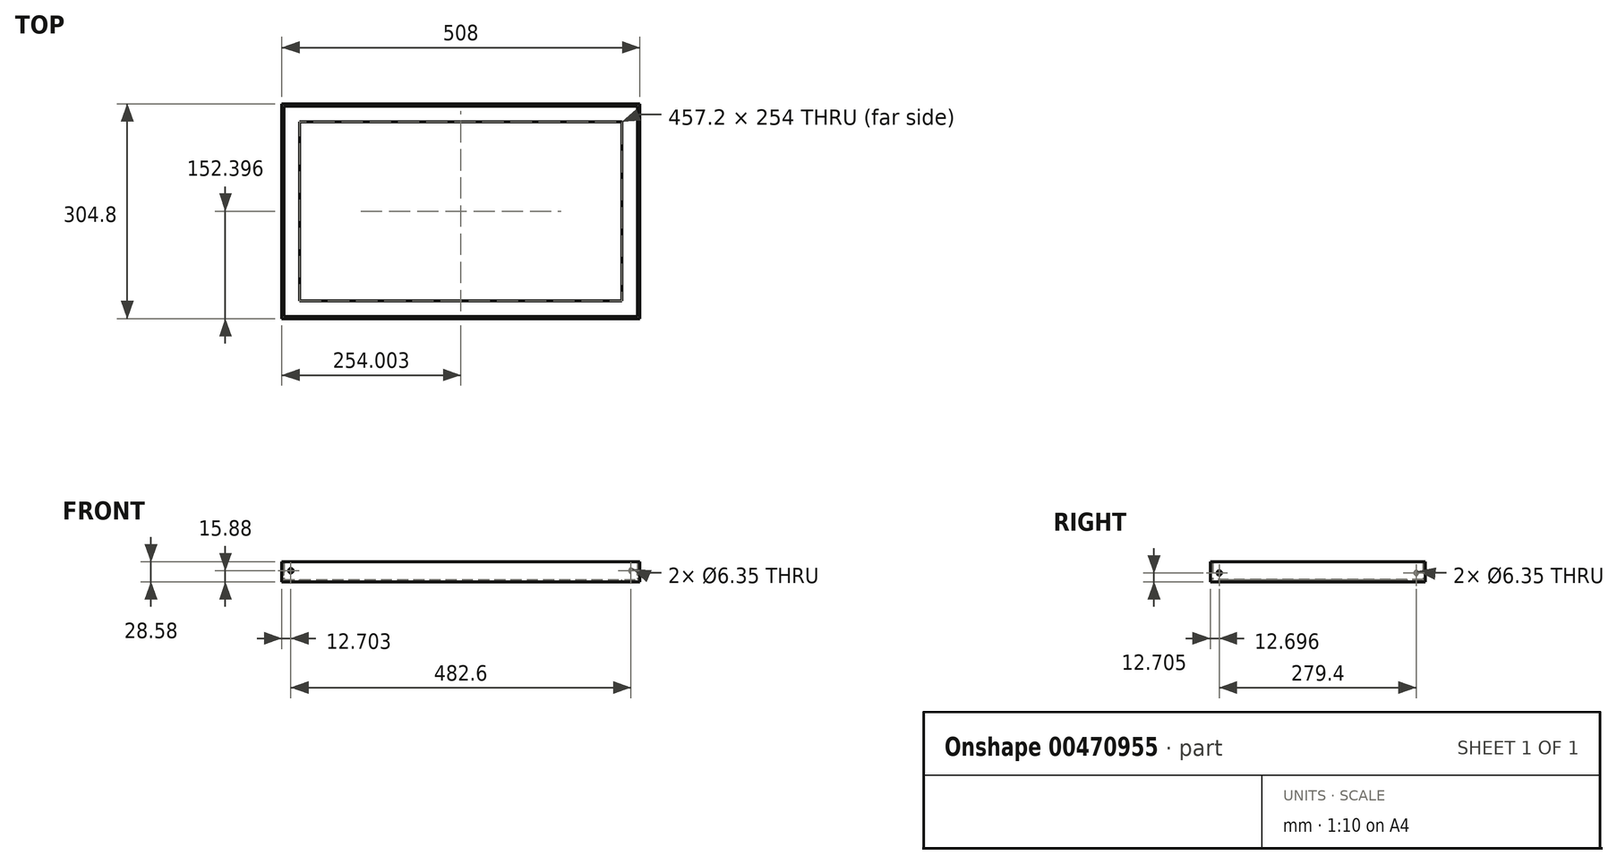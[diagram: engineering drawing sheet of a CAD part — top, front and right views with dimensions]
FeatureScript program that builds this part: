
annotation { "Feature Type Name" : "Feature", "Feature Type Description" : "" }
export const myFeature = defineFeature(function(context is Context, id is Id, definition is map)
    precondition{}
    {
        {
            var Q0;
            Q0=qCreatedBy(makeId("Top.planeOp"),FACE);
            var sketch = newSketch(context, id + "F0", { "sketchPlane" : qUnion([Q0])});
            skLineSegment(sketch, "E0.bottom", {"start": v(-258.98, 164.35) * mm, "end": v(249.02, 164.35) * mm});
            skLineSegment(sketch, "E0.top", {"start": v(-258.98, -140.45) * mm, "end": v(249.02, -140.45) * mm});
            skLineSegment(sketch, "E0.left", {"start": v(-258.98, 164.35) * mm, "end": v(-258.98, -140.45) * mm});
            skLineSegment(sketch, "E0.right", {"start": v(249.02, 164.35) * mm, "end": v(249.02, -140.45) * mm});
            skLineSegment(sketch, "E1.0", {"start": v(-255.8, 164.35) * mm, "end": v(-255.8, -140.45) * mm});
            skLineSegment(sketch, "E2.0", {"start": v(-258.98, -137.28) * mm, "end": v(249.02, -137.28) * mm});
            skLineSegment(sketch, "E3.0", {"start": v(245.85, 164.35) * mm, "end": v(245.85, -140.45) * mm});
            skLineSegment(sketch, "E4.0", {"start": v(-258.98, 161.17) * mm, "end": v(249.02, 161.17) * mm});
            skLineSegment(sketch, "E5.0", {"start": v(-233.58, 164.35) * mm, "end": v(-233.58, -140.45) * mm});
            skLineSegment(sketch, "E6.0", {"start": v(-258.98, -115.05) * mm, "end": v(249.02, -115.05) * mm});
            skLineSegment(sketch, "E7.0", {"start": v(223.62, 164.35) * mm, "end": v(223.62, -140.45) * mm});
            skLineSegment(sketch, "E8.0", {"start": v(-258.98, 138.95) * mm, "end": v(249.02, 138.95) * mm});
            skSolve(sketch);
        }
        {
            var Q0;
            {var subQ0=sQuery(id+"F0.wireOp",EDGE,"E6.0");var subQ1=sQuery(id+"F0.wireOp",EDGE,"E0.left");var subQ2=makeQuery(id+"F0.imprint","INTERSECT",VERTEX,{"derivedFrom":[subQ1,subQ0]});Q0=makeQuery(id+"F0.imprint","IMPRINT",FACE,{"disambiguationData":[TD([[makeQuery(id+"F0.imprint","IMPRINT",EDGE,{"disambiguationData":[TD([[subQ2,1.0]])],"derivedFrom":subQ1}),1.0]])]});}
            var Q1;
            {var subQ0=sQuery(id+"F0.wireOp",EDGE,"E2.0");var subQ1=sQuery(id+"F0.wireOp",EDGE,"E0.left");var subQ2=makeQuery(id+"F0.imprint","INTERSECT",VERTEX,{"derivedFrom":[subQ1,subQ0]});Q1=makeQuery(id+"F0.imprint","IMPRINT",FACE,{"disambiguationData":[TD([[makeQuery(id+"F0.imprint","IMPRINT",EDGE,{"disambiguationData":[TD([[subQ2,1.0]])],"derivedFrom":subQ1}),1.0]])]});}
            var Q2;
            {var subQ0=sQuery(id+"F0.wireOp",EDGE,"E0.left");var subQ1=sQuery(id+"F0.wireOp",EDGE,"E0.top");var subQ2=makeQuery(id+"F0.imprint","INTERSECT",VERTEX,{"derivedFrom":[subQ1,subQ0]});Q2=makeQuery(id+"F0.imprint","IMPRINT",FACE,{"disambiguationData":[TD([[makeQuery(id+"F0.imprint","IMPRINT",EDGE,{"disambiguationData":[TD([[subQ2,-1.0]])],"derivedFrom":subQ1}),1.0]])]});}
            var Q3;
            {var subQ0=sQuery(id+"F0.wireOp",EDGE,"E1.0");var subQ1=sQuery(id+"F0.wireOp",EDGE,"E0.top");var subQ2=makeQuery(id+"F0.imprint","INTERSECT",VERTEX,{"derivedFrom":[subQ1,subQ0]});Q3=makeQuery(id+"F0.imprint","IMPRINT",FACE,{"disambiguationData":[TD([[makeQuery(id+"F0.imprint","IMPRINT",EDGE,{"disambiguationData":[TD([[subQ2,-1.0]])],"derivedFrom":subQ1}),1.0]])]});}
            var Q4;
            {var subQ0=sQuery(id+"F0.wireOp",EDGE,"E5.0");var subQ1=sQuery(id+"F0.wireOp",EDGE,"E0.top");var subQ2=makeQuery(id+"F0.imprint","INTERSECT",VERTEX,{"derivedFrom":[subQ1,subQ0]});Q4=makeQuery(id+"F0.imprint","IMPRINT",FACE,{"disambiguationData":[TD([[makeQuery(id+"F0.imprint","IMPRINT",EDGE,{"disambiguationData":[TD([[subQ2,-1.0]])],"derivedFrom":subQ1}),1.0]])]});}
            var Q5;
            {var subQ0=sQuery(id+"F0.wireOp",EDGE,"E3.0");var subQ1=sQuery(id+"F0.wireOp",EDGE,"E0.top");var subQ2=makeQuery(id+"F0.imprint","INTERSECT",VERTEX,{"derivedFrom":[subQ1,subQ0]});Q5=makeQuery(id+"F0.imprint","IMPRINT",FACE,{"disambiguationData":[TD([[makeQuery(id+"F0.imprint","IMPRINT",EDGE,{"disambiguationData":[TD([[subQ2,1.0]])],"derivedFrom":subQ1}),1.0]])]});}
            var Q6;
            {var subQ0=sQuery(id+"F0.wireOp",EDGE,"E0.right");var subQ1=sQuery(id+"F0.wireOp",EDGE,"E0.top");var subQ2=makeQuery(id+"F0.imprint","INTERSECT",VERTEX,{"derivedFrom":[subQ1,subQ0]});Q6=makeQuery(id+"F0.imprint","IMPRINT",FACE,{"disambiguationData":[TD([[makeQuery(id+"F0.imprint","IMPRINT",EDGE,{"disambiguationData":[TD([[subQ2,1.0]])],"derivedFrom":subQ1}),1.0]])]});}
            var Q7;
            {var subQ0=sQuery(id+"F0.wireOp",EDGE,"E2.0");var subQ1=sQuery(id+"F0.wireOp",EDGE,"E0.right");var subQ2=makeQuery(id+"F0.imprint","INTERSECT",VERTEX,{"derivedFrom":[subQ1,subQ0]});Q7=makeQuery(id+"F0.imprint","IMPRINT",FACE,{"disambiguationData":[TD([[makeQuery(id+"F0.imprint","IMPRINT",EDGE,{"disambiguationData":[TD([[subQ2,1.0]])],"derivedFrom":subQ1}),-1.0]])]});}
            var Q8;
            {var subQ0=sQuery(id+"F0.wireOp",EDGE,"E6.0");var subQ1=sQuery(id+"F0.wireOp",EDGE,"E0.right");var subQ2=makeQuery(id+"F0.imprint","INTERSECT",VERTEX,{"derivedFrom":[subQ1,subQ0]});Q8=makeQuery(id+"F0.imprint","IMPRINT",FACE,{"disambiguationData":[TD([[makeQuery(id+"F0.imprint","IMPRINT",EDGE,{"disambiguationData":[TD([[subQ2,1.0]])],"derivedFrom":subQ1}),-1.0]])]});}
            var Q9;
            {var subQ0=sQuery(id+"F0.wireOp",EDGE,"E4.0");var subQ1=sQuery(id+"F0.wireOp",EDGE,"E0.right");var subQ2=makeQuery(id+"F0.imprint","INTERSECT",VERTEX,{"derivedFrom":[subQ1,subQ0]});Q9=makeQuery(id+"F0.imprint","IMPRINT",FACE,{"disambiguationData":[TD([[makeQuery(id+"F0.imprint","IMPRINT",EDGE,{"disambiguationData":[TD([[subQ2,-1.0]])],"derivedFrom":subQ1}),-1.0]])]});}
            var Q10;
            {var subQ0=sQuery(id+"F0.wireOp",EDGE,"E0.right");var subQ1=sQuery(id+"F0.wireOp",EDGE,"E0.bottom");var subQ2=makeQuery(id+"F0.imprint","INTERSECT",VERTEX,{"derivedFrom":[subQ1,subQ0]});Q10=makeQuery(id+"F0.imprint","IMPRINT",FACE,{"disambiguationData":[TD([[makeQuery(id+"F0.imprint","IMPRINT",EDGE,{"disambiguationData":[TD([[subQ2,1.0]])],"derivedFrom":subQ1}),-1.0]])]});}
            var Q11;
            {var subQ0=sQuery(id+"F0.wireOp",EDGE,"E3.0");var subQ1=sQuery(id+"F0.wireOp",EDGE,"E0.bottom");var subQ2=makeQuery(id+"F0.imprint","INTERSECT",VERTEX,{"derivedFrom":[subQ1,subQ0]});Q11=makeQuery(id+"F0.imprint","IMPRINT",FACE,{"disambiguationData":[TD([[makeQuery(id+"F0.imprint","IMPRINT",EDGE,{"disambiguationData":[TD([[subQ2,1.0]])],"derivedFrom":subQ1}),-1.0]])]});}
            var Q12;
            {var subQ0=sQuery(id+"F0.wireOp",EDGE,"E5.0");var subQ1=sQuery(id+"F0.wireOp",EDGE,"E0.bottom");var subQ2=makeQuery(id+"F0.imprint","INTERSECT",VERTEX,{"derivedFrom":[subQ1,subQ0]});Q12=makeQuery(id+"F0.imprint","IMPRINT",FACE,{"disambiguationData":[TD([[makeQuery(id+"F0.imprint","IMPRINT",EDGE,{"disambiguationData":[TD([[subQ2,-1.0]])],"derivedFrom":subQ1}),-1.0]])]});}
            var Q13;
            {var subQ0=sQuery(id+"F0.wireOp",EDGE,"E1.0");var subQ1=sQuery(id+"F0.wireOp",EDGE,"E0.bottom");var subQ2=makeQuery(id+"F0.imprint","INTERSECT",VERTEX,{"derivedFrom":[subQ1,subQ0]});Q13=makeQuery(id+"F0.imprint","IMPRINT",FACE,{"disambiguationData":[TD([[makeQuery(id+"F0.imprint","IMPRINT",EDGE,{"disambiguationData":[TD([[subQ2,-1.0]])],"derivedFrom":subQ1}),-1.0]])]});}
            var Q14;
            {var subQ0=sQuery(id+"F0.wireOp",EDGE,"E0.left");var subQ1=sQuery(id+"F0.wireOp",EDGE,"E0.bottom");var subQ2=makeQuery(id+"F0.imprint","INTERSECT",VERTEX,{"derivedFrom":[subQ1,subQ0]});Q14=makeQuery(id+"F0.imprint","IMPRINT",FACE,{"disambiguationData":[TD([[makeQuery(id+"F0.imprint","IMPRINT",EDGE,{"disambiguationData":[TD([[subQ2,-1.0]])],"derivedFrom":subQ1}),-1.0]])]});}
            var Q15;
            {var subQ0=sQuery(id+"F0.wireOp",EDGE,"E4.0");var subQ1=sQuery(id+"F0.wireOp",EDGE,"E0.left");var subQ2=makeQuery(id+"F0.imprint","INTERSECT",VERTEX,{"derivedFrom":[subQ1,subQ0]});Q15=makeQuery(id+"F0.imprint","IMPRINT",FACE,{"disambiguationData":[TD([[makeQuery(id+"F0.imprint","IMPRINT",EDGE,{"disambiguationData":[TD([[subQ2,-1.0]])],"derivedFrom":subQ1}),1.0]])]});}
            extrude(context, id + "F1", {"entities" : qUnion([Q0, Q1, Q2, Q3, Q4, Q5, Q6, Q7, Q8, Q9, Q10, Q11, Q12, Q13, Q14, Q15]), "depth" : 25.4 * mm});
        }
        {
            var Q0;
            Q0=makeQuery(id+"F1.opExtrude","CAP_FACE",FACE,{"disambiguationData":[OSD([sQuery(id+"F0.wireOp",EDGE,"E0.bottom"),sQuery(id+"F0.wireOp",EDGE,"E0.top"),sQuery(id+"F0.wireOp",EDGE,"E0.left"),sQuery(id+"F0.wireOp",EDGE,"E0.right"),sQuery(id+"F0.wireOp",EDGE,"E1.0"),sQuery(id+"F0.wireOp",EDGE,"E2.0"),sQuery(id+"F0.wireOp",EDGE,"E3.0"),sQuery(id+"F0.wireOp",EDGE,"E4.0")])],"isStart":true});
            var sketch = newSketch(context, id + "F2", { "sketchPlane" : qUnion([Q0])});
            skLineSegment(sketch, "E9.bottom", {"start": v(-258.98, 140.45) * mm, "end": v(249.02, 140.45) * mm});
            skLineSegment(sketch, "E9.top", {"start": v(-258.98, -164.35) * mm, "end": v(249.02, -164.35) * mm});
            skLineSegment(sketch, "E9.left", {"start": v(-258.98, 140.45) * mm, "end": v(-258.98, -164.35) * mm});
            skLineSegment(sketch, "E9.right", {"start": v(249.02, 140.45) * mm, "end": v(249.02, -164.35) * mm});
            skLineSegment(sketch, "E10.0", {"start": v(-233.58, 115.05) * mm, "end": v(223.62, 115.05) * mm});
            skLineSegment(sketch, "E11.0", {"start": v(-233.58, 115.05) * mm, "end": v(-233.58, -138.95) * mm});
            skLineSegment(sketch, "E12.0", {"start": v(-233.58, -138.95) * mm, "end": v(223.62, -138.95) * mm});
            skLineSegment(sketch, "E13.0", {"start": v(223.62, 115.05) * mm, "end": v(223.62, -138.95) * mm});
            skSolve(sketch);
        }
        {
            var Q0;
            Q0=makeQuery(id+"F2.imprint","IMPRINT",FACE,{"disambiguationData":[TD([[makeQuery(id+"F2.imprint","IMPRINT",EDGE,{"derivedFrom":sQuery(id+"F2.wireOp",EDGE,"E9.bottom")}),-1.0]])]});
            var Q1;
            Q1=makeQuery(id+"F2.imprint","IMPRINT",FACE,{"disambiguationData":[TD([[makeQuery(id+"F2.imprint","IMPRINT",EDGE,{"derivedFrom":sQuery(id+"F2.wireOp",EDGE,"E10.0")}),1.0]])]});
            extrude(context, id + "F3", {"entities" : qUnion([Q0, Q1]), "operationType" : NewBodyOperationType.ADD, "depth" : 3.17 * mm});
        }
        {
            var Q0;
            Q0=makeQuery(id+"F3.boolean.opBoolean","MERGE",FACE,{"derivedFrom":[makeQuery(id+"F1.opExtrude","SWEPT_FACE",FACE,{"disambiguationData":[OSD([sQuery(id+"F0.wireOp",EDGE,"E0.top")])]}),makeQuery(id+"F3.opExtrude","SWEPT_FACE",FACE,{"disambiguationData":[OSD([sQuery(id+"F2.wireOp",EDGE,"E9.bottom")])]})]});
            var sketch = newSketch(context, id + "F4", { "sketchPlane" : qUnion([Q0])});
            skPoint(sketch, "E14", {"position": v(-246.28, 12.7) * mm});
            skSolve(sketch);
        }
        {
            var Q0;
            Q0=sQuery(id+"F4.wireOp",VERTEX,"E14");
            var Q1;
            Q1=makeQuery(id+"F1.opExtrude","SWEPT_BODY",BODY,{"disambiguationData":[OSD([sQuery(id+"F0.wireOp",EDGE,"E0.bottom"),sQuery(id+"F0.wireOp",EDGE,"E0.top"),sQuery(id+"F0.wireOp",EDGE,"E0.left"),sQuery(id+"F0.wireOp",EDGE,"E0.right"),sQuery(id+"F0.wireOp",EDGE,"E1.0"),sQuery(id+"F0.wireOp",EDGE,"E2.0"),sQuery(id+"F0.wireOp",EDGE,"E3.0"),sQuery(id+"F0.wireOp",EDGE,"E4.0")])]});
            hole(context, id + "F5", {"style" : HoleStyle.SIMPLE, "endStyle" : HoleEndStyle.BLIND, "holeDiameter" : 6.35 * mm, "holeDepth" : 12.7 * mm, "tappedDepth" : 12.7 * mm, "tapClearance" : 3, "locations" : qUnion([Q0]), "scope" : qUnion([Q1])});
        }
        {
            var Q0;
            Q0=makeQuery(id+"F3.boolean.opBoolean","MERGE",FACE,{"derivedFrom":[makeQuery(id+"F1.opExtrude","SWEPT_FACE",FACE,{"disambiguationData":[OSD([sQuery(id+"F0.wireOp",EDGE,"E0.right")])]}),makeQuery(id+"F3.opExtrude","SWEPT_FACE",FACE,{"disambiguationData":[OSD([sQuery(id+"F2.wireOp",EDGE,"E9.right")])]})]});
            var sketch = newSketch(context, id + "F6", { "sketchPlane" : qUnion([Q0])});
            skPoint(sketch, "E15", {"position": v(-127.75, 9.53) * mm});
            skSolve(sketch);
        }
        {
            var Q0;
            Q0=sQuery(id+"F6.wireOp",VERTEX,"E15");
            var Q1;
            Q1=makeQuery(id+"F1.opExtrude","SWEPT_BODY",BODY,{"disambiguationData":[OSD([sQuery(id+"F0.wireOp",EDGE,"E0.bottom"),sQuery(id+"F0.wireOp",EDGE,"E0.top"),sQuery(id+"F0.wireOp",EDGE,"E0.left"),sQuery(id+"F0.wireOp",EDGE,"E0.right"),sQuery(id+"F0.wireOp",EDGE,"E1.0"),sQuery(id+"F0.wireOp",EDGE,"E2.0"),sQuery(id+"F0.wireOp",EDGE,"E3.0"),sQuery(id+"F0.wireOp",EDGE,"E4.0")])]});
            hole(context, id + "F7", {"style" : HoleStyle.SIMPLE, "endStyle" : HoleEndStyle.BLIND, "holeDiameter" : 6.35 * mm, "holeDepth" : 12.7 * mm, "tappedDepth" : 12.7 * mm, "tapClearance" : 3, "locations" : qUnion([Q0]), "scope" : qUnion([Q1])});
        }
        {
            var Q0;
            Q0=makeQuery(id+"F3.boolean.opBoolean","MERGE",FACE,{"derivedFrom":[makeQuery(id+"F1.opExtrude","SWEPT_FACE",FACE,{"disambiguationData":[OSD([sQuery(id+"F0.wireOp",EDGE,"E0.bottom")])]}),makeQuery(id+"F3.opExtrude","SWEPT_FACE",FACE,{"disambiguationData":[OSD([sQuery(id+"F2.wireOp",EDGE,"E9.top")])]})]});
            var sketch = newSketch(context, id + "F8", { "sketchPlane" : qUnion([Q0])});
            skPoint(sketch, "E16", {"position": v(-236.32, 12.7) * mm});
            skSolve(sketch);
        }
        {
            var Q0;
            Q0=sQuery(id+"F8.wireOp",VERTEX,"E16");
            var Q1;
            Q1=makeQuery(id+"F1.opExtrude","SWEPT_BODY",BODY,{"disambiguationData":[OSD([sQuery(id+"F0.wireOp",EDGE,"E0.bottom"),sQuery(id+"F0.wireOp",EDGE,"E0.top"),sQuery(id+"F0.wireOp",EDGE,"E0.left"),sQuery(id+"F0.wireOp",EDGE,"E0.right"),sQuery(id+"F0.wireOp",EDGE,"E1.0"),sQuery(id+"F0.wireOp",EDGE,"E2.0"),sQuery(id+"F0.wireOp",EDGE,"E3.0"),sQuery(id+"F0.wireOp",EDGE,"E4.0")])]});
            hole(context, id + "F9", {"style" : HoleStyle.SIMPLE, "endStyle" : HoleEndStyle.BLIND, "holeDiameter" : 6.35 * mm, "holeDepth" : 12.7 * mm, "tappedDepth" : 12.7 * mm, "tapClearance" : 3, "locations" : qUnion([Q0]), "scope" : qUnion([Q1])});
        }
        {
            var Q0;
            Q0=makeQuery(id+"F3.boolean.opBoolean","MERGE",FACE,{"derivedFrom":[makeQuery(id+"F1.opExtrude","SWEPT_FACE",FACE,{"disambiguationData":[OSD([sQuery(id+"F0.wireOp",EDGE,"E0.left")])]}),makeQuery(id+"F3.opExtrude","SWEPT_FACE",FACE,{"disambiguationData":[OSD([sQuery(id+"F2.wireOp",EDGE,"E9.left")])]})]});
            var sketch = newSketch(context, id + "F10", { "sketchPlane" : qUnion([Q0])});
            skPoint(sketch, "E17", {"position": v(-151.65, 9.53) * mm});
            skSolve(sketch);
        }
        {
            var Q0;
            Q0=sQuery(id+"F10.wireOp",VERTEX,"E17");
            var Q1;
            Q1=makeQuery(id+"F1.opExtrude","SWEPT_BODY",BODY,{"disambiguationData":[OSD([sQuery(id+"F0.wireOp",EDGE,"E0.bottom"),sQuery(id+"F0.wireOp",EDGE,"E0.top"),sQuery(id+"F0.wireOp",EDGE,"E0.left"),sQuery(id+"F0.wireOp",EDGE,"E0.right"),sQuery(id+"F0.wireOp",EDGE,"E1.0"),sQuery(id+"F0.wireOp",EDGE,"E2.0"),sQuery(id+"F0.wireOp",EDGE,"E3.0"),sQuery(id+"F0.wireOp",EDGE,"E4.0")])]});
            hole(context, id + "F11", {"style" : HoleStyle.SIMPLE, "endStyle" : HoleEndStyle.BLIND, "holeDiameter" : 6.35 * mm, "holeDepth" : 12.7 * mm, "tappedDepth" : 12.7 * mm, "tapClearance" : 3, "locations" : qUnion([Q0]), "scope" : qUnion([Q1])});
        }
    });
